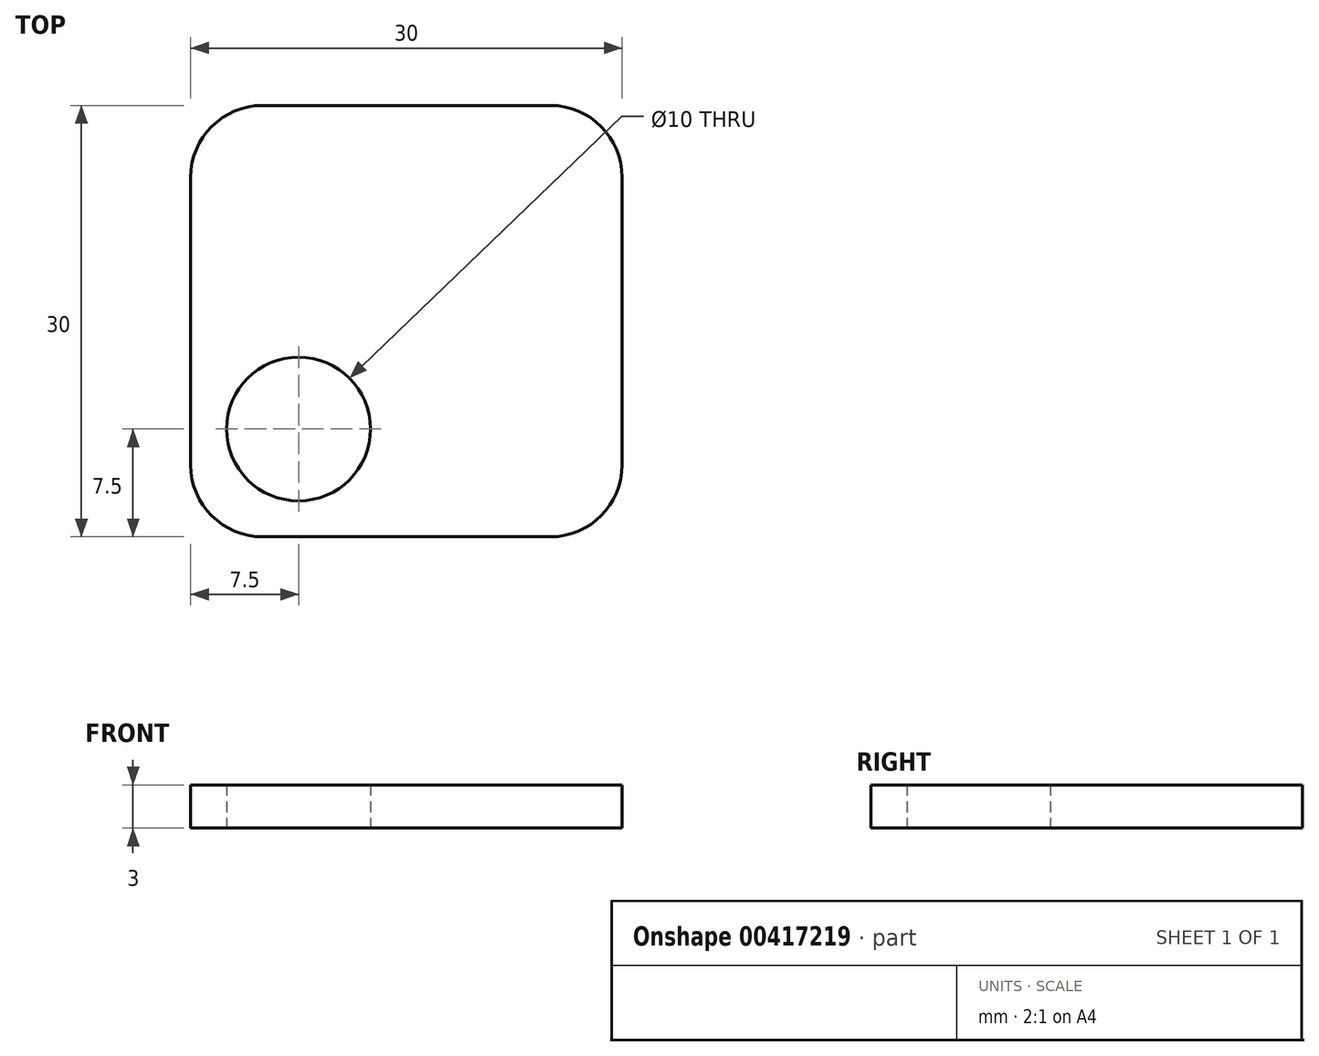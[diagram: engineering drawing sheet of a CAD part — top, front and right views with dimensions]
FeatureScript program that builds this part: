
annotation { "Feature Type Name" : "Feature", "Feature Type Description" : "" }
export const myFeature = defineFeature(function(context is Context, id is Id, definition is map)
    precondition{}
    {
        {
            var Q0;
            Q0=qCreatedBy(makeId("Top.planeOp"),FACE);
            var sketch = newSketch(context, id + "F0", { "sketchPlane" : qUnion([Q0])});
            skLineSegment(sketch, "E0.bottom", {"start": v(0, 0) * mm, "end": v(30, 0) * mm});
            skLineSegment(sketch, "E0.top", {"start": v(0, 30) * mm, "end": v(30, 30) * mm});
            skLineSegment(sketch, "E0.left", {"start": v(0, 0) * mm, "end": v(0, 30) * mm});
            skLineSegment(sketch, "E0.right", {"start": v(30, 0) * mm, "end": v(30, 30) * mm});
            skCircle(sketch, "E1", {"center": v(7.5, 7.5) * mm, "radius": 5 * mm});
            skCircle(sketch, "E2", {"center": v(7.5, 7.5) * mm, "radius": 7.5 * mm, "construction": true});
            skSolve(sketch);
        }
        {
            var Q0;
            Q0=makeQuery(id+"F0.imprint","IMPRINT",FACE,{"disambiguationData":[TD([[makeQuery(id+"F0.imprint","IMPRINT",EDGE,{"derivedFrom":sQuery(id+"F0.wireOp",EDGE,"E0.bottom")}),1.0]])]});
            extrude(context, id + "F1", {"entities" : qUnion([Q0]), "depth" : 3 * mm});
        }
        {
            var Q0;
            Q0=makeQuery(id+"F1.opExtrude","SWEPT_EDGE",EDGE,{"disambiguationData":[OSD([sQuery(id+"F0.wireOp",EDGE,"E0.bottom"),sQuery(id+"F0.wireOp",EDGE,"E0.right")])]});
            var Q1;
            Q1=makeQuery(id+"F1.opExtrude","SWEPT_EDGE",EDGE,{"disambiguationData":[OSD([sQuery(id+"F0.wireOp",EDGE,"E0.bottom"),sQuery(id+"F0.wireOp",EDGE,"E0.left")])]});
            var Q2;
            Q2=makeQuery(id+"F1.opExtrude","SWEPT_EDGE",EDGE,{"disambiguationData":[OSD([sQuery(id+"F0.wireOp",EDGE,"E0.top"),sQuery(id+"F0.wireOp",EDGE,"E0.right")])]});
            var Q3;
            Q3=makeQuery(id+"F1.opExtrude","SWEPT_EDGE",EDGE,{"disambiguationData":[OSD([sQuery(id+"F0.wireOp",EDGE,"E0.top"),sQuery(id+"F0.wireOp",EDGE,"E0.left")])]});
            fillet(context, id + "F2", {"entities" : qUnion([Q0, Q1, Q2, Q3]), "radius" : 5 * mm, "tangentPropagation" : true, "allowEdgeOverflow" : false});
        }
    });
